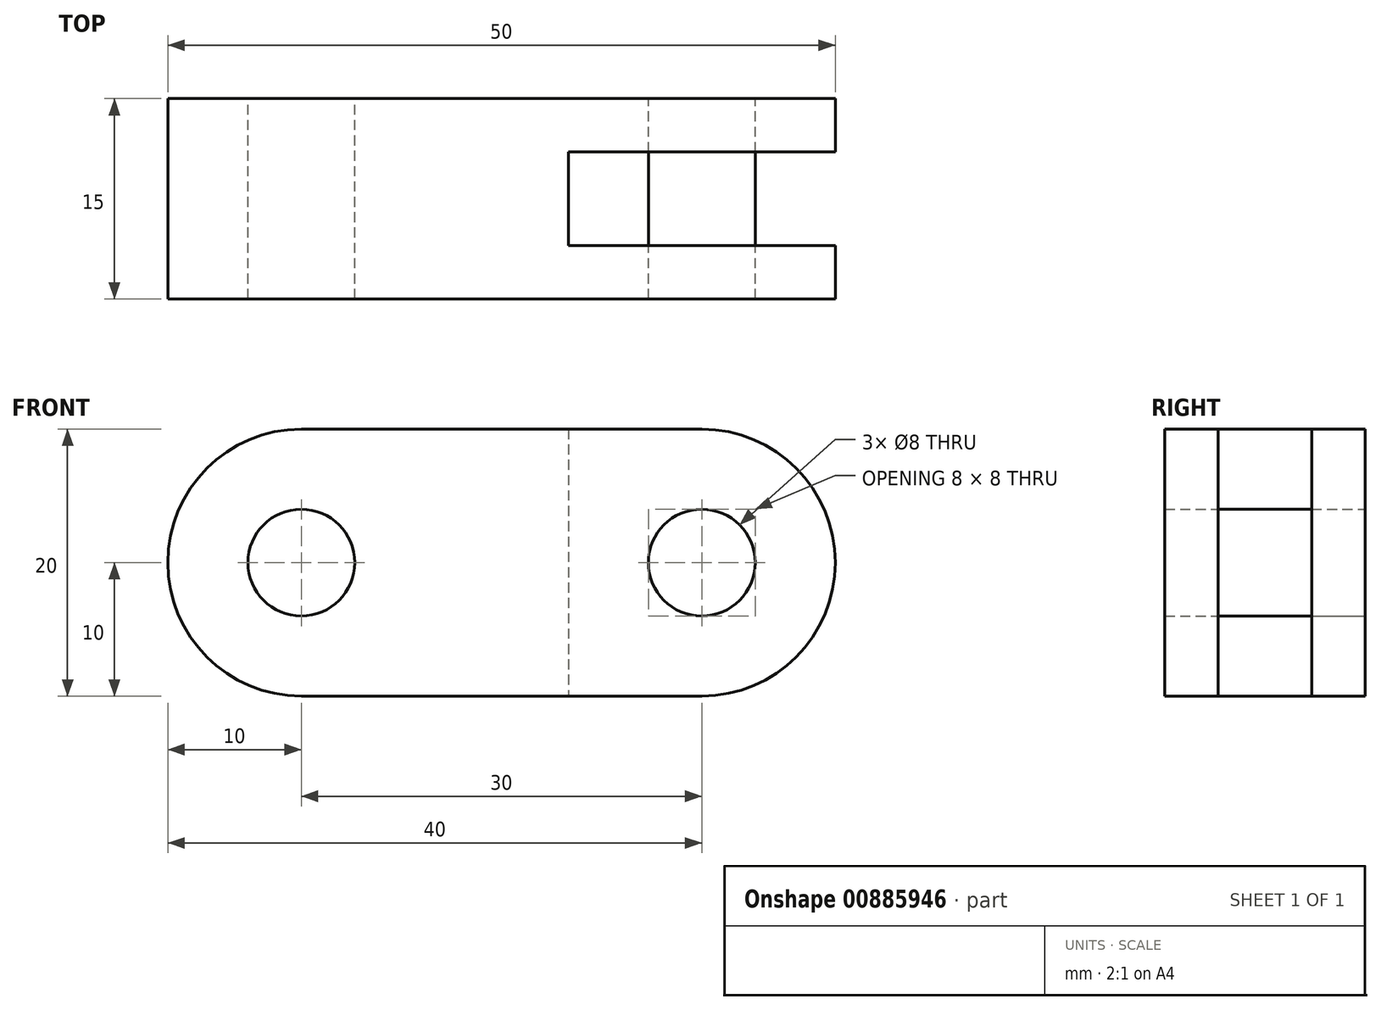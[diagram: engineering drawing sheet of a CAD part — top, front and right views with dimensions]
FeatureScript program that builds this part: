
annotation { "Feature Type Name" : "Feature", "Feature Type Description" : "" }
export const myFeature = defineFeature(function(context is Context, id is Id, definition is map)
    precondition{}
    {
        {
            var Q0;
            Q0=qCreatedBy(makeId("Front.planeOp"),FACE);
            var sketch = newSketch(context, id + "F0", { "sketchPlane" : qUnion([Q0])});
            skLineSegment(sketch, "E0", {"start": v(0, 52.63) * mm, "end": v(0, -59.42) * mm, "construction": true});
            skLineSegment(sketch, "E1", {"start": v(-47.03, 0) * mm, "end": v(62.95, 0) * mm, "construction": true});
            skLineSegment(sketch, "E2.bottom", {"start": v(-15, 10) * mm, "end": v(15, 10) * mm});
            skLineSegment(sketch, "E2.top", {"start": v(-15, -10) * mm, "end": v(15, -10) * mm});
            skArc(sketch, "E3", {"start": v(-15, 10) * mm, "mid": v(-25, 0) * mm, "end": v(-15, -10) * mm});
            skArc(sketch, "E4", {"start": v(15, -10) * mm, "mid": v(25, 0) * mm, "end": v(15, 10) * mm});
            skCircle(sketch, "E5", {"center": v(15, 0) * mm, "radius": 4 * mm});
            skCircle(sketch, "E6", {"center": v(-15, 0) * mm, "radius": 4 * mm});
            skSolve(sketch);
        }
        {
            var Q0;
            Q0=makeQuery(id+"F0.imprint","IMPRINT",FACE,{"disambiguationData":[TD([[makeQuery(id+"F0.imprint","IMPRINT",EDGE,{"derivedFrom":sQuery(id+"F0.wireOp",EDGE,"E2.bottom")}),-1.0]])]});
            extrude(context, id + "F1", {"entities" : qUnion([Q0]), "depth" : 15 * mm, "offsetDistance" : 25 * mm, "symmetric" : true});
        }
        {
            var Q0;
            Q0=makeQuery(id+"F1.opExtrude","SWEPT_FACE",FACE,{"disambiguationData":[OSD([sQuery(id+"F0.wireOp",EDGE,"E2.top")])]});
            var sketch = newSketch(context, id + "F2", { "sketchPlane" : qUnion([Q0])});
            skLineSegment(sketch, "E7", {"start": v(38.76, 0) * mm, "end": v(7.23, 0) * mm, "construction": true});
            skLineSegment(sketch, "E8", {"start": v(25, 7.5) * mm, "end": v(25, -7.5) * mm, "construction": true});
            skLineSegment(sketch, "E9.bottom", {"start": v(5, 3.5) * mm, "end": v(28.54, 3.5) * mm});
            skLineSegment(sketch, "E9.top", {"start": v(5, -3.5) * mm, "end": v(28.54, -3.5) * mm});
            skLineSegment(sketch, "E9.left", {"start": v(5, 3.5) * mm, "end": v(5, -3.5) * mm});
            skLineSegment(sketch, "E9.right", {"start": v(28.54, 3.5) * mm, "end": v(28.54, -3.5) * mm});
            skSolve(sketch);
        }
        {
            var Q0;
            {var subQ0=sQuery(id+"F2.wireOp",EDGE,"E9.right");Q0=makeQuery(id+"F2.imprint","IMPRINT",FACE,{"disambiguationData":[TD([[makeQuery(id+"F2.imprint","IMPRINT",EDGE,{"derivedFrom":subQ0}),-1.0]])]});}
            var Q1;
            {var subQ0=sQuery(id+"F2.wireOp",EDGE,"E9.left");Q1=makeQuery(id+"F2.imprint","IMPRINT",FACE,{"disambiguationData":[TD([[makeQuery(id+"F2.imprint","IMPRINT",EDGE,{"derivedFrom":subQ0}),1.0]])]});}
            extrude(context, id + "F3", {"entities" : qUnion([Q0, Q1]), "operationType" : NewBodyOperationType.REMOVE, "endBound" : BoundingType.THROUGH_ALL, "oppositeDirection" : true, "depth" : 25 * mm, "offsetDistance" : 25 * mm});
        }
        {
            var Q0;
            Q0=makeQuery(id+"F1.opExtrude","CAP_FACE",FACE,{"disambiguationData":[OSD([sQuery(id+"F0.wireOp",EDGE,"E2.bottom"),sQuery(id+"F0.wireOp",EDGE,"E2.top"),sQuery(id+"F0.wireOp",EDGE,"E3"),sQuery(id+"F0.wireOp",EDGE,"E4"),sQuery(id+"F0.wireOp",EDGE,"E5"),sQuery(id+"F0.wireOp",EDGE,"E6")])],"isStart":true});
            var sketch = newSketch(context, id + "F4", { "sketchPlane" : qUnion([Q0])});
            skCircle(sketch, "E10.0", {"center": v(-15, 0) * mm, "radius": 4 * mm, "construction": true});
            skCircle(sketch, "E11.0", {"center": v(15, 0) * mm, "radius": 4 * mm, "construction": true});
            skCircle(sketch, "E12", {"center": v(-15, 0) * mm, "radius": 4 * mm});
            skCircle(sketch, "E13", {"center": v(15, 0) * mm, "radius": 4 * mm});
            skSolve(sketch);
        }
        {
            var Q0;
            Q0 = qSketchRegion(id + "F4", true);
            extrude(context, id + "F5", {"entities" : qUnion([Q0]), "oppositeDirection" : true, "depth" : 15 * mm, "offsetDistance" : 25 * mm});
        }
        {
            var Q0;
            Q0=makeQuery(id+"F5.opExtrude","SWEPT_BODY",BODY,{"disambiguationData":[OSD([sQuery(id+"F4.wireOp",EDGE,"E13")])]});
            deleteBodies(context, id + "F6", {"entities" : qUnion([Q0])});
        }
    });
